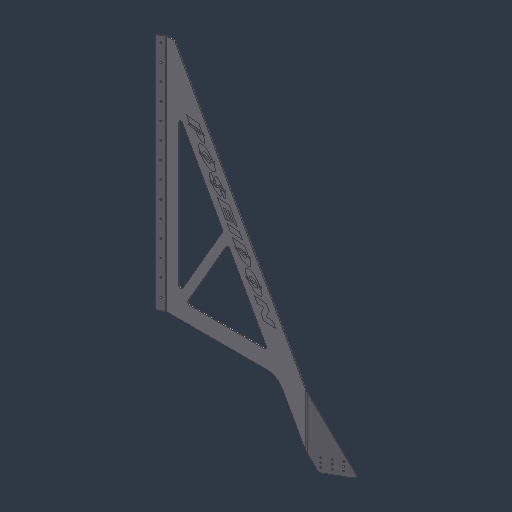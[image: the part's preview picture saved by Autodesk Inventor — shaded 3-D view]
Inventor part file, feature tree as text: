
AUTODESK INVENTOR PART (.ipt)
format: ipt  version: 2024.3 (Build 283343000, 343)  size: 827,392 bytes
history: native  units: mm (DEFAULTED — no unit token found)
features: sketch x5, sheet_metal_op x5, other x3, extrude x2, hole x2, pattern_linear x1, plane x1, chamfer x1, projected_geometry x1
ambient origin geometry x8: Origin, YZ Plane, XZ Plane, XY Plane, X Axis, Y Axis, Z Axis, Center Point
bodies: Solid7 (feature_tree), Solid8 (feature_tree)
feature tree (21):
  sketch  "Sketch1"  dims[d0=25.4mm d1=917.575mm]
  sheet_metal_op  "Face1"
  extrude  "Extrusion2"  Depth=917.575mm
  extrude  "Extrusion3"  Depth=533.4mm
  sheet_metal_op  "Flange1"
  sketch  "Sketch4"  dims[d4=203.2mm d5=38.1mm]
  hole  "Hole2"  [1 undecoded]
  pattern_linear  "Rectangular Pattern2"  Spacing1=0.0mm  [1 undecoded]
  plane  "Work Plane1"
  sheet_metal_op  "Fold2"
  hole  "Hole3"  [1 undecoded]
  chamfer  "Corner Round1"
  other  "Plate1"
  sketch  "Sketch3"  dims[d2=76.2mm d3=533.4mm]
  other  "Plate2"
  sheet_metal_op  "Bend1"
  sheet_metal_op  "Corner1"
  sketch  "Sketch5"  dims[d7=50.8mm]
  sketch  "Sketch6"  dims[d10=3.175mm d11=0.0mm d12=0.0mm d13=9.948377mm d14=12.7mm d15=4.7625mm d16=30.0mm d18=66.04mm d19=10.0mm d21=25.4mm d23=20.0mm d25=285.75mm d26=10.0mm d28=25.4mm d30=20.0mm d32=69.85mm d33=10.0mm d35=25.4mm d37=3.175mm d38=0.0mm d55=25.4mm d56=60.0deg d57=6.35mm d58=50.8mm d62=19.05mm d63=19.05mm d65=3.175mm d66=1.5875mm d67=6.35mm d68=4.7625mm d69=25.4mm d70=30.0deg d71=4.7625mm d72=12.7mm d73=3.175mm d74=4.7625mm d75=12.7mm d76=19.05mm d84=5.1054mm d85=19.05mm d86=9.779mm d87=1.9558mm d88=14.3117mm d89=3.175mm d90=20.594885mm d98=-209.55mm d99=3.175mm d100=1.5875mm d101=6.35mm d102=4.7625mm d103=30.0deg d104=4.7625mm d105=419.1mm d106=189.286027mm d107=30.0mm d109=25.4mm d110=30.0mm d112=12.7mm d115=5.1054mm d116=19.05mm d117=9.779mm d118=6.35mm d119=14.3117mm d120=25.4mm d121=20.594885mm d125=140.0mm d127=50.8mm d128=12.7mm d129=0.872665mm d130=12.7mm d131=0.872665mm]
  projected_geometry  "Project Cut Edges1"
  other  "Definition1"
note: 3 required parameter values undecoded (feature->parameter linkage not recoverable at this tier; creation-order binding heuristic only, values carry confidence <= 0.55)
